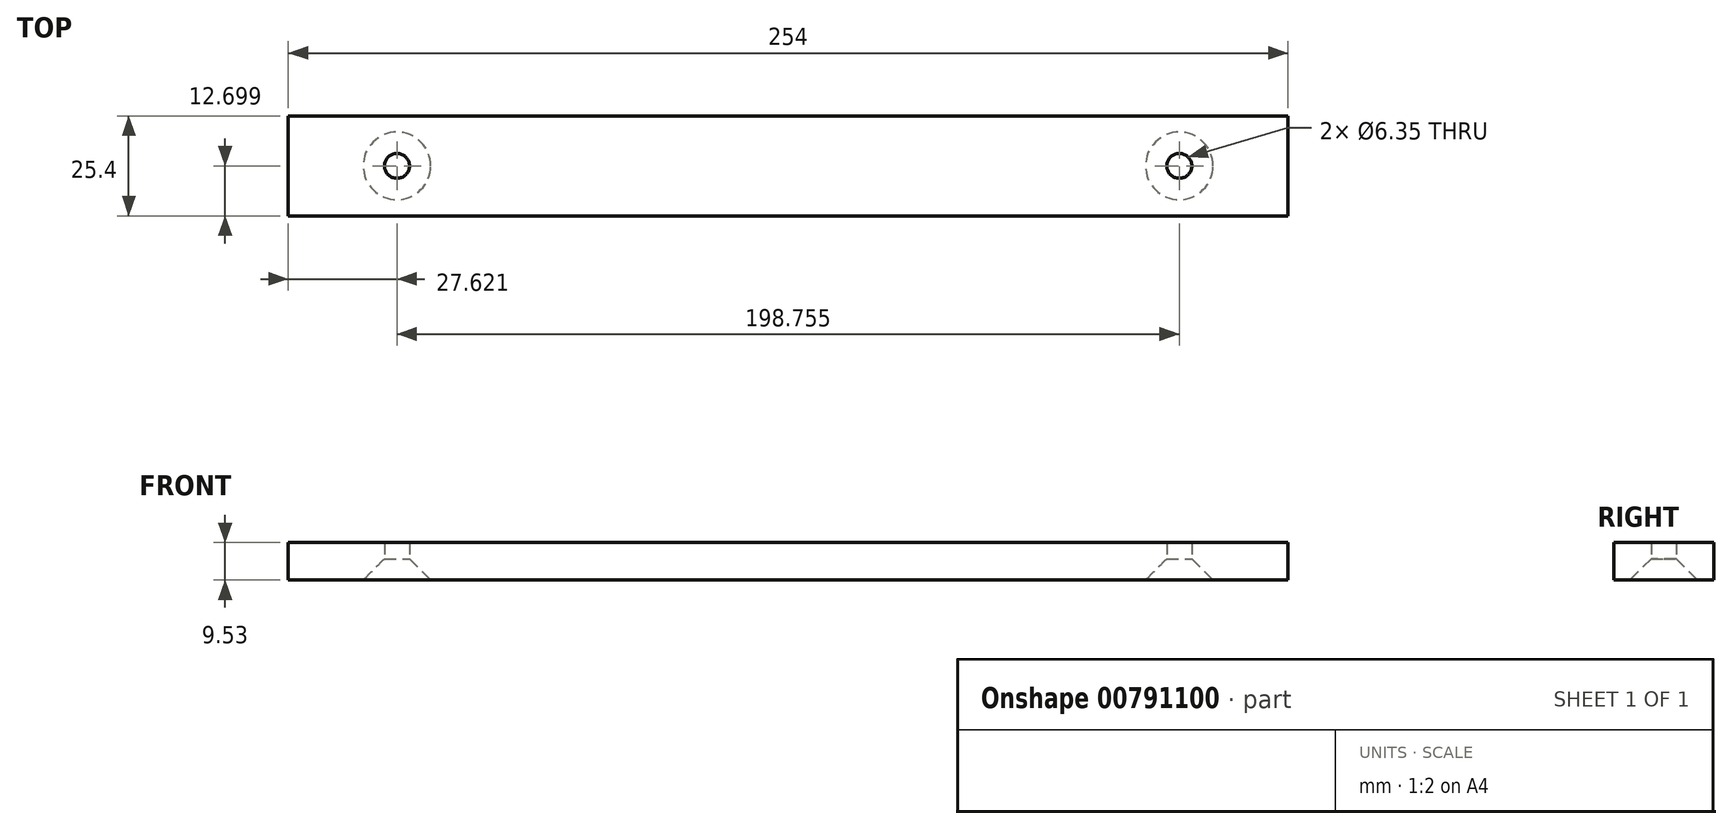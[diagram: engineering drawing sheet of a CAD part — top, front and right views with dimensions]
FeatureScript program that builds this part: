
annotation { "Feature Type Name" : "Feature", "Feature Type Description" : "" }
export const myFeature = defineFeature(function(context is Context, id is Id, definition is map)
    precondition{}
    {
        {
            var Q0;
            Q0=qCreatedBy(makeId("Top.planeOp"),FACE);
            var sketch = newSketch(context, id + "F0", { "sketchPlane" : qUnion([Q0])});
            skLineSegment(sketch, "E0.bottom", {"start": v(-114.4, 34.86) * mm, "end": v(139.6, 34.86) * mm});
            skLineSegment(sketch, "E0.top", {"start": v(-114.4, 9.46) * mm, "end": v(139.6, 9.46) * mm});
            skLineSegment(sketch, "E0.left", {"start": v(-114.4, 34.86) * mm, "end": v(-114.4, 9.46) * mm});
            skLineSegment(sketch, "E0.right", {"start": v(139.6, 34.86) * mm, "end": v(139.6, 9.46) * mm});
            skPoint(sketch, "E1", {"position": v(-95.34, 22.16) * mm});
            skPoint(sketch, "E1.positionSnap0", {"position": v(-114.4, 22.16) * mm});
            skPoint(sketch, "E2", {"position": v(120.56, 22.16) * mm});
            skPoint(sketch, "E2.positionSnap0", {"position": v(139.6, 22.16) * mm});
            skPoint(sketch, "E3", {"position": v(-78.2, 22.16) * mm});
            skPoint(sketch, "E4", {"position": v(103.41, 22.16) * mm});
            skPoint(sketch, "E5", {"position": v(111.99, 22.16) * mm});
            skPoint(sketch, "E6", {"position": v(-86.77, 22.16) * mm});
            skSolve(sketch);
        }
        {
            var Q0;
            Q0=makeQuery(id+"F0.imprint","IMPRINT",FACE,{"disambiguationData":[TD([[makeQuery(id+"F0.imprint","IMPRINT",EDGE,{"derivedFrom":sQuery(id+"F0.wireOp",EDGE,"E0.bottom")}),-1.0]])]});
            extrude(context, id + "F1", {"entities" : qUnion([Q0]), "depth" : 9.52 * mm, "offsetDistance" : 25.4 * mm});
        }
        {
            var Q0;
            Q0=sQuery(id+"F0.wireOp",VERTEX,"E6");
            var Q1;
            Q1=sQuery(id+"F0.wireOp",VERTEX,"E5");
            var Q2;
            Q2=makeQuery(id+"F1.opExtrude","SWEPT_BODY",BODY,{"disambiguationData":[OSD([sQuery(id+"F0.wireOp",EDGE,"E0.bottom"),sQuery(id+"F0.wireOp",EDGE,"E0.top"),sQuery(id+"F0.wireOp",EDGE,"E0.left"),sQuery(id+"F0.wireOp",EDGE,"E0.right")])]});
            hole(context, id + "F2", {"style" : HoleStyle.C_SINK, "endStyle" : HoleEndStyle.BLIND, "oppositeDirection" : true, "holeDiameter" : 6.35 * mm, "cSinkDiameter" : 17.14 * mm, "cSinkAngle" : 90 * degree, "majorDiameter" : 6.35 * mm, "holeDepth" : 9.52 * mm, "isTappedThrough" : true, "tappedDepth" : 12.7 * mm, "tapClearance" : 3, "locations" : qUnion([Q0, Q1]), "scope" : qUnion([Q2])});
        }
    });
